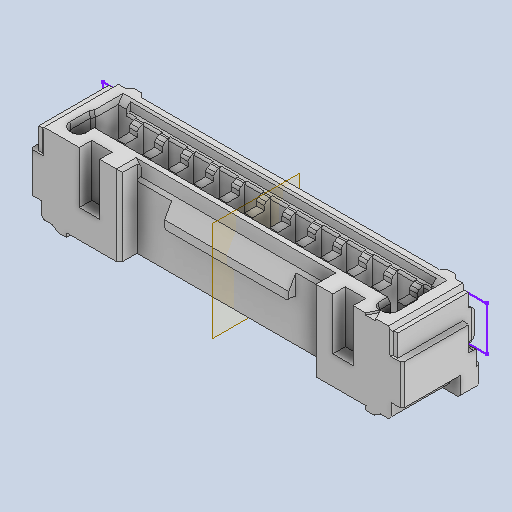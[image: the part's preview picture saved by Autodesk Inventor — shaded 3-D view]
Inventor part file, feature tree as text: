
AUTODESK INVENTOR PART (.ipt)
format: ipt  version: 2024.2 (Build 282272000, 272)  size: 530,432 bytes
history: native  units: mm
features: other x1, imported_body x1, plane x1, sketch x1
ambient origin geometry x8: Origin, YZ Plane, XZ Plane, XY Plane, X Axis, Y Axis, Z Axis, Center Point
bodies: Solid1 (feature_tree)
feature tree (4):
  other  "Repaired Geometry1"
  imported_body  "Base1"
  plane  "Work Plane1"
  sketch  "3D Sketch1"
